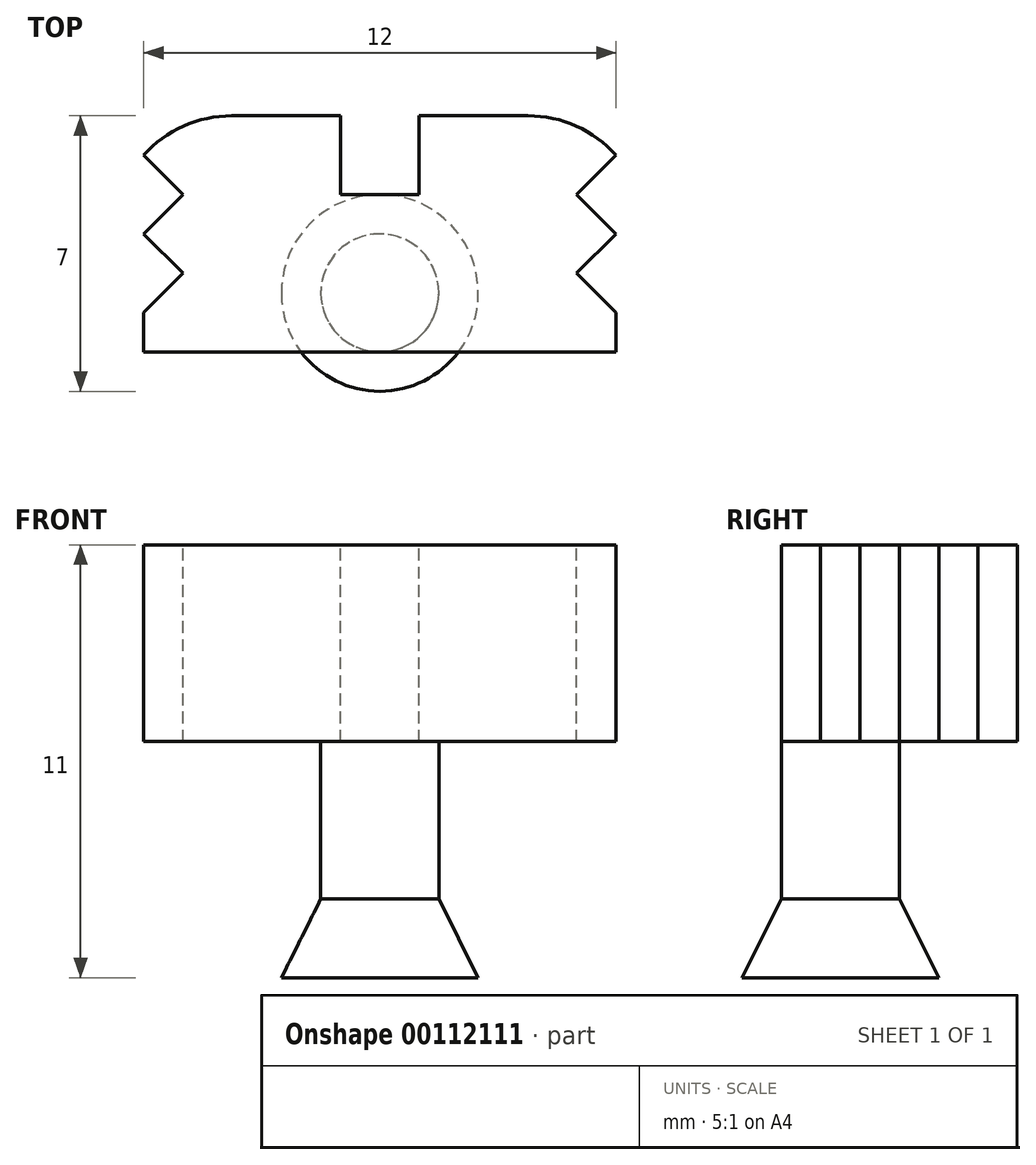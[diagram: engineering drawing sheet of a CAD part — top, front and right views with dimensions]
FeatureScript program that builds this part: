
annotation { "Feature Type Name" : "Feature", "Feature Type Description" : "" }
export const myFeature = defineFeature(function(context is Context, id is Id, definition is map)
    precondition{}
    {
        {
            var Q0;
            Q0=qCreatedBy(makeId("Top.planeOp"),FACE);
            var sketch = newSketch(context, id + "F0", { "sketchPlane" : qUnion([Q0])});
            skLineSegment(sketch, "E0.bottom", {"start": v(6, -3) * mm, "end": v(-6, -3) * mm});
            skLineSegment(sketch, "E0.top", {"start": v(6, 3) * mm, "end": v(1, 3) * mm});
            skLineSegment(sketch, "E0.left", {"start": v(6, -3) * mm, "end": v(6, 3) * mm});
            skLineSegment(sketch, "E0.right", {"start": v(-6, -3) * mm, "end": v(-6, 3) * mm});
            skPoint(sketch, "E0.middle", {"position": v(0, 0) * mm});
            skLineSegment(sketch, "E1.top", {"start": v(1, 1) * mm, "end": v(-1, 1) * mm});
            skLineSegment(sketch, "E1.left", {"start": v(1, 3) * mm, "end": v(1, 1) * mm});
            skLineSegment(sketch, "E1.right", {"start": v(-1, 3) * mm, "end": v(-1, 1) * mm});
            skPoint(sketch, "E1.middle", {"position": v(0, 2) * mm});
            skPoint(sketch, "E1.middle.positionSnap0", {"position": v(0, 3) * mm});
            skPoint(sketch, "E1.centerSnap0", {"position": v(0, 3) * mm});
            skLineSegment(sketch, "E2.trimOffspring", {"start": v(-1, 3) * mm, "end": v(-6, 3) * mm});
            skLineSegment(sketch, "E3", {"start": v(-1, 3) * mm, "end": v(1, 3) * mm});
            skSolve(sketch);
        }
        {
            var Q0;
            Q0 = qSketchRegion(id + "F0", true);
            extrude(context, id + "F1", {"entities" : qUnion([Q0]), "depth" : 5 * mm});
        }
        {
            var Q0;
            Q0=makeQuery(id+"F1.opExtrude","CAP_FACE",FACE,{"disambiguationData":[OSD([sQuery(id+"F0.wireOp",EDGE,"E0.bottom"),sQuery(id+"F0.wireOp",EDGE,"E0.top"),sQuery(id+"F0.wireOp",EDGE,"E0.left"),sQuery(id+"F0.wireOp",EDGE,"E0.right"),sQuery(id+"F0.wireOp",EDGE,"E1.top"),sQuery(id+"F0.wireOp",EDGE,"E1.left"),sQuery(id+"F0.wireOp",EDGE,"E1.right"),sQuery(id+"F0.wireOp",EDGE,"E2.trimOffspring")])],"isStart":true});
            var sketch = newSketch(context, id + "F2", { "sketchPlane" : qUnion([Q0])});
            skLineSegment(sketch, "E4.0", {"start": v(6, 3) * mm, "end": v(-6, 3) * mm});
            skLineSegment(sketch, "E5.bottom", {"start": v(1.5, 3) * mm, "end": v(-1.5, 3) * mm});
            skLineSegment(sketch, "E5.top", {"start": v(1.5, 0) * mm, "end": v(-1.5, 0) * mm});
            skLineSegment(sketch, "E5.left", {"start": v(1.5, 3) * mm, "end": v(1.5, 0) * mm});
            skLineSegment(sketch, "E5.right", {"start": v(-1.5, 3) * mm, "end": v(-1.5, 0) * mm});
            skPoint(sketch, "E5.middle", {"position": v(0, 1.5) * mm});
            skSolve(sketch);
        }
        {
            var Q0;
            Q0 = qSketchRegion(id + "F2", true);
            extrude(context, id + "F3", {"entities" : qUnion([Q0]), "operationType" : NewBodyOperationType.ADD, "depth" : 4 * mm});
        }
        {
            var Q0;
            Q0=makeQuery(id+"F3.opExtrude","SWEPT_EDGE",EDGE,{"disambiguationData":[OSD([sQuery(id+"F2.wireOp",EDGE,"E5.top"),sQuery(id+"F2.wireOp",EDGE,"E5.right")])]});
            var Q1;
            Q1=makeQuery(id+"F3.opExtrude","SWEPT_EDGE",EDGE,{"disambiguationData":[OSD([sQuery(id+"F2.wireOp",EDGE,"E5.top"),sQuery(id+"F2.wireOp",EDGE,"E5.left")])]});
            var Q2;
            Q2=makeQuery(id+"F3.opExtrude","SWEPT_EDGE",EDGE,{"disambiguationData":[OSD([sQuery(id+"F2.wireOp",EDGE,"E4.0"),sQuery(id+"F2.wireOp",EDGE,"E5.bottom"),sQuery(id+"F2.wireOp",EDGE,"E5.right")])]});
            var Q3;
            Q3=makeQuery(id+"F3.opExtrude","SWEPT_EDGE",EDGE,{"disambiguationData":[OSD([sQuery(id+"F2.wireOp",EDGE,"E4.0"),sQuery(id+"F2.wireOp",EDGE,"E5.bottom"),sQuery(id+"F2.wireOp",EDGE,"E5.left")])]});
            fillet(context, id + "F4", {"entities" : qUnion([Q0, Q1, Q2, Q3]), "radius" : 1.5 * mm, "tangentPropagation" : true, "allowEdgeOverflow" : false});
        }
        {
            var Q0;
            Q0=makeQuery(id+"F1.opExtrude","CAP_FACE",FACE,{"disambiguationData":[OSD([sQuery(id+"F0.wireOp",EDGE,"E0.bottom"),sQuery(id+"F0.wireOp",EDGE,"E0.top"),sQuery(id+"F0.wireOp",EDGE,"E0.left"),sQuery(id+"F0.wireOp",EDGE,"E0.right"),sQuery(id+"F0.wireOp",EDGE,"E2.trimOffspring"),sQuery(id+"F0.wireOp",EDGE,"E3")])],"isStart":false});
            var sketch = newSketch(context, id + "F5", { "sketchPlane" : qUnion([Q0])});
            skLineSegment(sketch, "E6.bottom", {"start": v(-1, 3) * mm, "end": v(1, 3) * mm});
            skLineSegment(sketch, "E6.top", {"start": v(-1, 1) * mm, "end": v(1, 1) * mm});
            skLineSegment(sketch, "E6.left", {"start": v(-1, 3) * mm, "end": v(-1, 1) * mm});
            skLineSegment(sketch, "E6.right", {"start": v(1, 3) * mm, "end": v(1, 1) * mm});
            skPoint(sketch, "E6.middle", {"position": v(0, 2) * mm});
            skPoint(sketch, "E6.middle.positionSnap0", {"position": v(0, 3) * mm});
            skPoint(sketch, "E6.centerSnap0", {"position": v(0, 3) * mm});
            skSolve(sketch);
        }
        {
            var Q0;
            Q0 = qSketchRegion(id + "F5", true);
            extrude(context, id + "F6", {"entities" : qUnion([Q0]), "operationType" : NewBodyOperationType.REMOVE, "endBound" : BoundingType.UP_TO_NEXT, "oppositeDirection" : true, "depth" : 25 * mm});
        }
        {
            var Q0;
            Q0=makeQuery(id+"F1.opExtrude","CAP_FACE",FACE,{"disambiguationData":[OSD([sQuery(id+"F0.wireOp",EDGE,"E0.bottom"),sQuery(id+"F0.wireOp",EDGE,"E0.top"),sQuery(id+"F0.wireOp",EDGE,"E0.left"),sQuery(id+"F0.wireOp",EDGE,"E0.right"),sQuery(id+"F0.wireOp",EDGE,"E2.trimOffspring"),sQuery(id+"F0.wireOp",EDGE,"E3")])],"isStart":false});
            var sketch = newSketch(context, id + "F7", { "sketchPlane" : qUnion([Q0])});
            skLineSegment(sketch, "E7.0.0", {"start": v(-1, 1) * mm, "end": v(-1, 3) * mm});
            skLineSegment(sketch, "E7.0.1", {"start": v(-1, 3) * mm, "end": v(-6, 3) * mm});
            skLineSegment(sketch, "E7.0.2", {"start": v(-6, 3) * mm, "end": v(-6, -3) * mm});
            skLineSegment(sketch, "E7.0.3", {"start": v(-6, -3) * mm, "end": v(6, -3) * mm});
            skLineSegment(sketch, "E7.0.4", {"start": v(6, -3) * mm, "end": v(6, 3) * mm});
            skLineSegment(sketch, "E7.0.5", {"start": v(6, 3) * mm, "end": v(1, 3) * mm});
            skLineSegment(sketch, "E7.0.6", {"start": v(1, 3) * mm, "end": v(1, 1) * mm});
            skLineSegment(sketch, "E7.0.7", {"start": v(1, 1) * mm, "end": v(-1, 1) * mm});
            skLineSegment(sketch, "E8", {"start": v(-6, -2) * mm, "end": v(-5, -1) * mm});
            skLineSegment(sketch, "E9", {"start": v(-5, -1) * mm, "end": v(-6, 0) * mm});
            skLineSegment(sketch, "E10", {"start": v(-6, 0) * mm, "end": v(-5, 1) * mm});
            skLineSegment(sketch, "E11", {"start": v(-5, 1) * mm, "end": v(-6, 2) * mm});
            skLineSegment(sketch, "E12", {"start": v(0, 0) * mm, "end": v(0, -0.52) * mm});
            skLineSegment(sketch, "E13.MirrorCS", {"start": v(6, -2) * mm, "end": v(5, -1) * mm});
            skLineSegment(sketch, "E14.MirrorCS", {"start": v(5, -1) * mm, "end": v(6, 0) * mm});
            skLineSegment(sketch, "E15.MirrorCS", {"start": v(6, 0) * mm, "end": v(5, 1) * mm});
            skLineSegment(sketch, "E16.MirrorCS", {"start": v(5, 1) * mm, "end": v(6, 2) * mm});
            skSolve(sketch);
        }
        {
            var Q0;
            {var subQ0=sQuery(id+"F7.wireOp",EDGE,"E10");Q0=makeQuery(id+"F7.imprint","IMPRINT",FACE,{"disambiguationData":[TD([[makeQuery(id+"F7.imprint","IMPRINT",EDGE,{"derivedFrom":subQ0}),1.0]])]});}
            var Q1;
            {var subQ0=sQuery(id+"F7.wireOp",EDGE,"E8");Q1=makeQuery(id+"F7.imprint","IMPRINT",FACE,{"disambiguationData":[TD([[makeQuery(id+"F7.imprint","IMPRINT",EDGE,{"derivedFrom":subQ0}),1.0]])]});}
            var Q2;
            {var subQ0=sQuery(id+"F7.wireOp",EDGE,"E13.MirrorCS");Q2=makeQuery(id+"F7.imprint","IMPRINT",FACE,{"disambiguationData":[TD([[makeQuery(id+"F7.imprint","IMPRINT",EDGE,{"derivedFrom":subQ0}),-1.0]])]});}
            var Q3;
            {var subQ0=sQuery(id+"F7.wireOp",EDGE,"E15.MirrorCS");Q3=makeQuery(id+"F7.imprint","IMPRINT",FACE,{"disambiguationData":[TD([[makeQuery(id+"F7.imprint","IMPRINT",EDGE,{"derivedFrom":subQ0}),-1.0]])]});}
            extrude(context, id + "F8", {"entities" : qUnion([Q0, Q1, Q2, Q3]), "operationType" : NewBodyOperationType.REMOVE, "endBound" : BoundingType.THROUGH_ALL, "oppositeDirection" : true, "depth" : 25 * mm});
        }
        {
            var Q0;
            Q0=makeQuery(id+"F1.opExtrude","SWEPT_EDGE",EDGE,{"disambiguationData":[OSD([sQuery(id+"F0.wireOp",EDGE,"E0.right"),sQuery(id+"F0.wireOp",EDGE,"E2.trimOffspring")])]});
            var Q1;
            Q1=makeQuery(id+"F1.opExtrude","SWEPT_EDGE",EDGE,{"disambiguationData":[OSD([sQuery(id+"F0.wireOp",EDGE,"E0.top"),sQuery(id+"F0.wireOp",EDGE,"E0.left")])]});
            fillet(context, id + "F9", {"entities" : qUnion([Q0, Q1]), "radius" : 3 * mm, "tangentPropagation" : true, "allowEdgeOverflow" : false});
        }
        {
            var Q0;
            Q0=makeQuery(id+"F3.opExtrude","CAP_FACE",FACE,{"disambiguationData":[OSD([sQuery(id+"F2.wireOp",EDGE,"E5.bottom"),sQuery(id+"F2.wireOp",EDGE,"E5.top"),sQuery(id+"F2.wireOp",EDGE,"E5.left"),sQuery(id+"F2.wireOp",EDGE,"E5.right")])],"isStart":false});
            var sketch = newSketch(context, id + "F10", { "sketchPlane" : qUnion([Q0])});
            skCircle(sketch, "E17.0.0", {"center": v(0, 1.5) * mm, "radius": 1.5 * mm});
            skSolve(sketch);
        }
        {
            var Q0;
            Q0=makeQuery(id+"F10.imprint","IMPRINT",FACE,{"disambiguationData":[TD([[makeQuery(id+"F10.imprint","IMPRINT",EDGE,{"derivedFrom":sQuery(id+"F10.wireOp",EDGE,"E17.0.0")}),1.0]])]});
            cPlane(context, id + "F11", {"entities" : qUnion([Q0]), "cplaneType" : CPlaneType.OFFSET, "offset" : 2 * mm, "width" : 150 * mm, "height" : 150 * mm});
        }
        {
            var Q0;
            Q0=qCreatedBy(id+"F11.planeOp",FACE);
            var sketch = newSketch(context, id + "F12", { "sketchPlane" : qUnion([Q0])});
            skPoint(sketch, "E18.0", {"position": v(0, 1.5) * mm});
            skCircle(sketch, "E19", {"center": v(0, 1.5) * mm, "radius": 2.5 * mm});
            skSolve(sketch);
        }
        {
            var Q1;
            Q1 = qSketchRegion(id + "F10", true);
            var Q2;
            Q2 = qSketchRegion(id + "F12", true);
            loft(context, id + "F13", {"operationType" : NewBodyOperationType.ADD, "sheetProfilesArray" : [{ "sheetProfileEntities" : qUnion([Q1]) }, { "sheetProfileEntities" : qUnion([Q2]) }]});
        }
    });
